# Revit family: Cabinet_Specialty-Cabinet_File-Cabinet_Moduline
name_source: partatom
category: Furniture
units: mm (PartAtom-declared; Revit-internal decimal feet)

## family parameters
Always vertical = Yes
Cut with Voids When Loaded = No
Enable Cutting in Views = No
OmniClass Number = 23.40.20.00
OmniClass Title = General Furniture and Specialties
Render Appearance Source = Family Geometry
Room Calculation Point = No
Shared = No
Work Plane-Based = No

## types (2) — shared parameters
Depth = 24 "
Drawer Clearance = 20.75 "
Handle Length = 12.5 "
Keynote = 12 35 00
Manufacturer = Moduline Aluminum Cabinets
Model = Pro II Specialty Cabinets
Product Page URL = https://www.arcat.com
URL = https://modulinecabinets.com
Width = 16 "
zero-valued in all types: Default Elevation

## per-type parameters (varying)
| type | 3 Drawers | 4 Drawers | Description | Height |
| 36"H x 24"D x 16"W | No | Yes | Modular Specialty Cabinet, File Cabinet, 36" Height x 24" Depth x 16" Width | 35.875 " |
| 32"H x 24"D x 16"W | Yes | No | Modular Specialty Cabinet, File Cabinet, 32" Height x 24" Depth x 16" Width | 31.875 " |

## geometry (parser evidence)
native form markers: Sweep x4
no freeform markers — native parametric forms only
